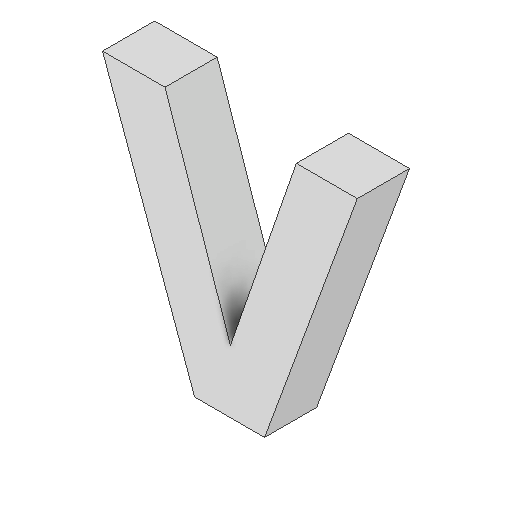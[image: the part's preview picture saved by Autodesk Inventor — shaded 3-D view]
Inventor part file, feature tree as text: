
AUTODESK INVENTOR PART (.ipt)
format: ipt  version: 2025 (Build 290162000, 162)  size: 116,224 bytes
history: native  units: mm
features: reference x7, extrude x2, sketch x2, other x2, projected_geometry x1
ambient origin geometry x8: Origin, YZ Plane, XZ Plane, XY Plane, X Axis, Y Axis, Z Axis, Center Point
bodies: Solid1 (feature_tree)
feature tree (14):
  extrude  "Extrusion1"  Depth=1.4mm TaperAngle=0.0deg
  extrude  "Extrusion2"  Depth=10.0mm TaperAngle=0.0deg
  sketch  "Sketch1"  dims[d0=40.0mm d1=1.4mm d2=0.0mm]
  sketch  "Sketch2"  dims[d3=0.1mm d4=10.0mm d5=0.0mm]
  projected_geometry  "Projected Loop1"
  reference  "Reference1"
  reference  "Reference2"
  reference  "Reference3"
  reference  "Reference4"
  reference  "Reference5"
  reference  "Reference6"
  reference  "Reference7"
  other  "USB_C_PD_PPS_sink_with_enclosure.iam"
  other  "display_cover_2:1"
